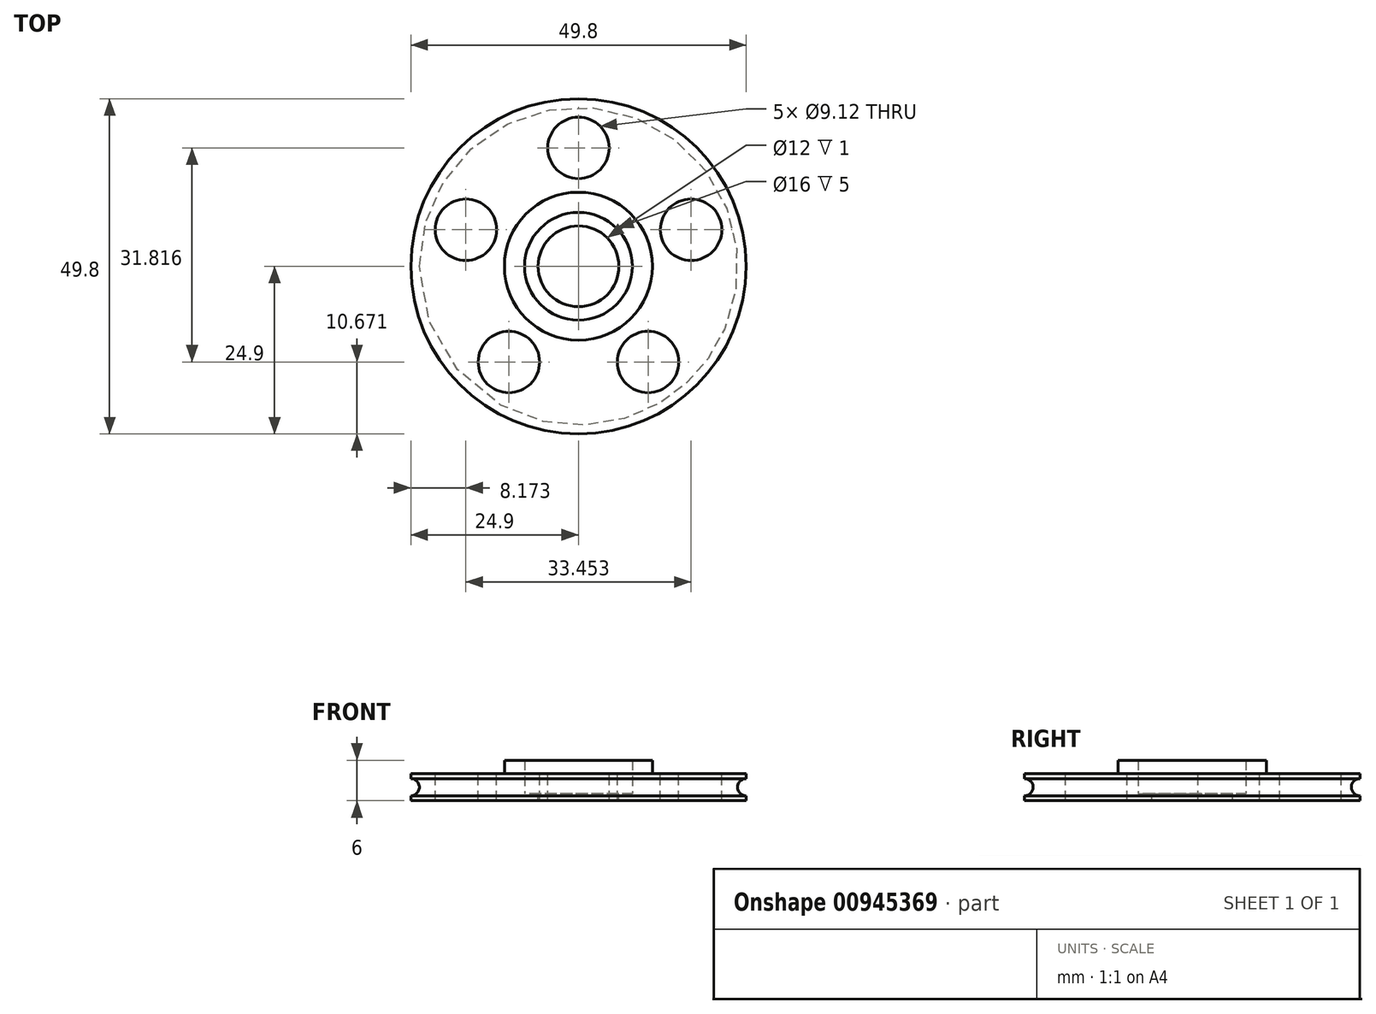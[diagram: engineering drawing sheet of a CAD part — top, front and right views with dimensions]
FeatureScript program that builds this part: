
annotation { "Feature Type Name" : "Feature", "Feature Type Description" : "" }
export const myFeature = defineFeature(function(context is Context, id is Id, definition is map)
    precondition{}
    {
        {
            var Q0;
            Q0=qCreatedBy(makeId("Top.planeOp"),FACE);
            var sketch = newSketch(context, id + "F0", { "sketchPlane" : qUnion([Q0])});
            skCircle(sketch, "E0", {"center": v(0, 0) * mm, "radius": 24.9 * mm});
            skSolve(sketch);
        }
        {
            var Q0;
            Q0=makeQuery(id+"F0.imprint","IMPRINT",FACE,{"disambiguationData":[TD([[makeQuery(id+"F0.imprint","IMPRINT",EDGE,{"derivedFrom":sQuery(id+"F0.wireOp",EDGE,"E0")}),1.0]])]});
            extrude(context, id + "F1", {"entities" : qUnion([Q0]), "depth" : 4 * mm, "offsetDistance" : 25.4 * mm});
        }
        {
            var Q0;
            Q0=makeQuery(id+"F1.opExtrude","CAP_FACE",FACE,{"disambiguationData":[OSD([sQuery(id+"F0.wireOp",EDGE,"E0"),sQuery(id+"F0.wireOp",EDGE,"n39IqKt5-bk1q-LU1x-fgod-8OyBNiFTd7FZ")])],"isStart":false});
            var sketch = newSketch(context, id + "F2", { "sketchPlane" : qUnion([Q0])});
            skCircle(sketch, "E1", {"center": v(0, 0) * mm, "radius": 8 * mm});
            skCircle(sketch, "E2.0", {"center": v(0, 0) * mm, "radius": 11 * mm});
            skSolve(sketch);
        }
        {
            var Q0;
            Q0=qSketchRegion(id+"F2",true);
            extrude(context, id + "F3", {"entities" : qUnion([Q0]), "operationType" : NewBodyOperationType.ADD, "depth" : 2 * mm, "offsetDistance" : 25.4 * mm});
        }
        {
            var Q0;
            Q0=makeQuery(id+"F3.boolean.opBoolean","SPLIT",FACE,{"disambiguationData":[TD([makeQuery(id+"F3.opExtrude","SWEPT_FACE",FACE,{"disambiguationData":[OSD([sQuery(id+"F2.wireOp",EDGE,"E1")])]})])],"derivedFrom":makeQuery(id+"F1.opExtrude","CAP_FACE",FACE,{"disambiguationData":[OSD([sQuery(id+"F0.wireOp",EDGE,"E0")])],"isStart":false})});
            var sketch = newSketch(context, id + "F4", { "sketchPlane" : qUnion([Q0])});
            skCircle(sketch, "E3", {"center": v(0, 0) * mm, "radius": 6 * mm});
            skSolve(sketch);
        }
        {
            var Q0;
            Q0=makeQuery(id+"F4.imprint","IMPRINT",FACE,{"disambiguationData":[TD([[makeQuery(id+"F4.imprint","IMPRINT",EDGE,{"derivedFrom":sQuery(id+"F4.wireOp",EDGE,"E3")}),1.0]])]});
            var Q1;
            Q1=makeQuery(id+"F4.imprint","IMPRINT",FACE,{"disambiguationData":[TD([[makeQuery(id+"F4.imprint","IMPRINT",EDGE,{"derivedFrom":makeQuery(id+"FgYK8jIepfClWtA_1.opExtrude","CAP_EDGE",EDGE,{"disambiguationData":[OSD([sQuery(id+"F8DXjnVyigKkjng_1.wireOp",EDGE,"EUjAMsCd-Zx2B-3j4q-cP5o-T3GrjTijNDqK")])],"isStart":false})}),1.0]])]});
            extrude(context, id + "F5", {"entities" : qUnion([Q0, Q1]), "operationType" : NewBodyOperationType.REMOVE, "oppositeDirection" : true, "depth" : 9 * mm, "offsetDistance" : 25.4 * mm});
        }
        {
            var Q0;
            Q0=qCreatedBy(makeId("Front.planeOp"),FACE);
            var sketch = newSketch(context, id + "F6", { "sketchPlane" : qUnion([Q0])});
            skCircle(sketch, "E4", {"center": v(-27.3, 2) * mm, "radius": 1.5 * mm});
            skLineSegment(sketch, "E5.bottom", {"start": v(-25.8, 0.65) * mm, "end": v(-27.95, 0.65) * mm});
            skLineSegment(sketch, "E5.top", {"start": v(-25.8, 3.35) * mm, "end": v(-27.95, 3.35) * mm});
            skLineSegment(sketch, "E5.left", {"start": v(-25.8, 0.65) * mm, "end": v(-25.8, 3.35) * mm});
            skLineSegment(sketch, "E5.right", {"start": v(-28.8, 1.91) * mm, "end": v(-28.8, 2.09) * mm});
            skLineSegment(sketch, "E6", {"start": v(0, 19.1) * mm, "end": v(0, -12.61) * mm, "construction": true});
            skLineSegment(sketch, "E7", {"start": v(-25.8, 1.83) * mm, "end": v(-25.81, 1.83) * mm});
            skPoint(sketch, "E8.orphan", {"position": v(-38.97, 3.35) * mm});
            skPoint(sketch, "E9.end.orphan", {"position": v(-15.64, 0.65) * mm});
            skPoint(sketch, "E9.start.orphan", {"position": v(-25.8, 2) * mm});
            skSolve(sketch);
        }
        {
            var Q0;
            {var subQ0=sQuery(id+"F6.wireOp",EDGE,"E5.top");var subQ1=sQuery(id+"F6.wireOp",EDGE,"E4");var subQ2=makeQuery(id+"F6.imprint","INTERSECT",VERTEX,{"disambiguationData":[OD(0.0)],"derivedFrom":[subQ1,subQ0]});Q0=makeQuery(id+"F6.imprint","IMPRINT",FACE,{"disambiguationData":[TD([[makeQuery(id+"F6.imprint","IMPRINT",EDGE,{"disambiguationData":[TD([[subQ2,1.0]])],"derivedFrom":subQ1}),1.0]])]});}
            var Q1;
            {var subQ0=sQuery(id+"F6.wireOp",EDGE,"E5.bottom");var subQ1=sQuery(id+"F6.wireOp",EDGE,"E4");var subQ2=makeQuery(id+"F6.imprint","INTERSECT",VERTEX,{"disambiguationData":[OD(0.0)],"derivedFrom":[subQ1,subQ0]});Q1=makeQuery(id+"F6.imprint","IMPRINT",FACE,{"disambiguationData":[TD([[makeQuery(id+"F6.imprint","IMPRINT",EDGE,{"disambiguationData":[TD([[subQ2,-1.0]])],"derivedFrom":subQ1}),1.0]])]});}
            var Q2;
            {var subQ4=sQuery(id+"F6.wireOp",EDGE,"E5.right");Q2=makeQuery(id+"F6.imprint","IMPRINT",FACE,{"disambiguationData":[TD([[makeQuery(id+"F6.imprint","IMPRINT",EDGE,{"derivedFrom":subQ4}),-1.0]])]});}
            var Q3;
            {var subQ0=sQuery(id+"F6.wireOp",EDGE,"p3G3spWP-JurA-dj01-Cwvm-HHlCDoPDIoxd");Q3=makeQuery(id+"F6.imprint","IMPRINT",FACE,{"disambiguationData":[TD([[makeQuery(id+"F6.imprint","IMPRINT",EDGE,{"derivedFrom":subQ0}),1.0]])]});}
            var Q4;
            Q4=makeQuery(id+"F6.imprint","IMPRINT",FACE,{"disambiguationData":[TD([[makeQuery(id+"F6.imprint","IMPRINT",EDGE,{"derivedFrom":sQuery(id+"F6.wireOp",EDGE,"p3G3spWP-JurA-dj01-Cwvm-HHlCDoPDIoxd")}),-1.0]])]});
            var Q5;
            {var subQ0=sQuery(id+"F6.wireOp",EDGE,"E9");Q5=makeQuery(id+"F6.imprint","IMPRINT",FACE,{"disambiguationData":[TD([[makeQuery(id+"F6.imprint","IMPRINT",EDGE,{"derivedFrom":subQ0}),1.0]])]});}
            var Q6;
            Q6=sQuery(id+"F6.wireOp",EDGE,"E6");
            revolve(context, id + "F7", {"operationType" : NewBodyOperationType.REMOVE, "surfaceOperationType" : NewSurfaceOperationType.NEW, "entities" : qUnion([Q0, Q1, Q2, Q3, Q4, Q5]), "axis" : qUnion([Q6]), "revolveType" : RevolveType.FULL, "oppositeDirection" : true});
        }
        {
            var Q0;
            Q0=makeQuery(id+"F3.boolean.opBoolean","SPLIT",FACE,{"disambiguationData":[TD([makeQuery(id+"F3.opExtrude","SWEPT_FACE",FACE,{"disambiguationData":[OSD([sQuery(id+"F2.wireOp",EDGE,"E1")])]})])],"derivedFrom":makeQuery(id+"F1.opExtrude","CAP_FACE",FACE,{"disambiguationData":[OSD([sQuery(id+"F0.wireOp",EDGE,"E0")])],"isStart":false})});
            extrude(context, id + "F8", {"entities" : qUnion([Q0]), "operationType" : NewBodyOperationType.REMOVE, "oppositeDirection" : true, "depth" : 3 * mm, "offsetDistance" : 25 * mm});
        }
        {
            var Q0;
            Q0=qCreatedBy(makeId("Front.planeOp"),FACE);
            var sketch = newSketch(context, id + "F9", { "sketchPlane" : qUnion([Q0])});
            skLineSegment(sketch, "E10", {"start": v(-24.92, 4) * mm, "end": v(-24.92, 0) * mm});
            skCircle(sketch, "E11", {"center": v(-24.92, 2) * mm, "radius": 1.28 * mm});
            skLineSegment(sketch, "E12", {"start": v(0, 9.34) * mm, "end": v(0, -3.6) * mm, "construction": true});
            skSolve(sketch);
        }
        {
            var Q0;
            {var subQ0=sQuery(id+"F9.wireOp",EDGE,"E11");var subQ1=sQuery(id+"F9.wireOp",EDGE,"E10");var subQ2=makeQuery(id+"F9.imprint","INTERSECT",VERTEX,{"disambiguationData":[OD(0.0)],"derivedFrom":[subQ1,subQ0]});Q0=makeQuery(id+"F9.imprint","IMPRINT",FACE,{"disambiguationData":[TD([[makeQuery(id+"F9.imprint","IMPRINT",EDGE,{"disambiguationData":[TD([[subQ2,1.0]])],"derivedFrom":subQ1}),1.0]])]});}
            var Q1;
            {var subQ0=sQuery(id+"F9.wireOp",EDGE,"E11");var subQ1=sQuery(id+"F9.wireOp",EDGE,"E10");var subQ2=makeQuery(id+"F9.imprint","INTERSECT",VERTEX,{"disambiguationData":[OD(0.0)],"derivedFrom":[subQ1,subQ0]});Q1=makeQuery(id+"F9.imprint","IMPRINT",FACE,{"disambiguationData":[TD([[makeQuery(id+"F9.imprint","IMPRINT",EDGE,{"disambiguationData":[TD([[subQ2,1.0]])],"derivedFrom":subQ1}),-1.0]])]});}
            var Q2;
            Q2=sQuery(id+"F9.wireOp",EDGE,"E12");
            revolve(context, id + "F10", {"operationType" : NewBodyOperationType.REMOVE, "surfaceOperationType" : NewSurfaceOperationType.NEW, "entities" : qUnion([Q0, Q1]), "axis" : qUnion([Q2]), "revolveType" : RevolveType.FULL, "oppositeDirection" : true});
        }
        {
            var Q0;
            {var subQ1=sQuery(id+"F0.wireOp",EDGE,"E0");var subQ2=makeQuery(id+"F1.opExtrude","SWEPT_FACE",FACE,{"disambiguationData":[OSD([subQ1])]});Q0=makeQuery(id+"FvaswZWDLJZ7FP9_1.boolean.opBoolean","SPLIT",FACE,{"disambiguationData":[TD([subQ2])],"derivedFrom":makeQuery(id+"F3.boolean.opBoolean","SPLIT",FACE,{"disambiguationData":[TD([subQ2])],"derivedFrom":makeQuery(id+"F1.opExtrude","CAP_FACE",FACE,{"disambiguationData":[OSD([subQ1])],"isStart":false})})});}
            var sketch = newSketch(context, id + "F11", { "sketchPlane" : qUnion([Q0])});
            skCircle(sketch, "E13", {"center": v(0, 17.59) * mm, "radius": 4.56 * mm});
            skCircle(sketch, "E14.1.0", {"center": v(-16.73, 5.43) * mm, "radius": 4.56 * mm});
            skCircle(sketch, "E14.2.0", {"center": v(-10.34, -14.23) * mm, "radius": 4.56 * mm});
            skCircle(sketch, "E14.3.0", {"center": v(10.34, -14.23) * mm, "radius": 4.56 * mm});
            skCircle(sketch, "E14.4.0", {"center": v(16.73, 5.43) * mm, "radius": 4.56 * mm});
            skPoint(sketch, "E14.center", {"position": v(0, 0) * mm});
            skSolve(sketch);
        }
        {
            var Q0;
            Q0=makeQuery(id+"F11.imprint","IMPRINT",FACE,{"disambiguationData":[TD([[makeQuery(id+"F11.imprint","IMPRINT",EDGE,{"derivedFrom":sQuery(id+"F11.wireOp",EDGE,"E13")}),1.0]])]});
            var Q1;
            Q1=makeQuery(id+"F11.imprint","IMPRINT",FACE,{"disambiguationData":[TD([[makeQuery(id+"F11.imprint","IMPRINT",EDGE,{"derivedFrom":sQuery(id+"F11.wireOp",EDGE,"E14.1.0")}),1.0]])]});
            var Q2;
            Q2=makeQuery(id+"F11.imprint","IMPRINT",FACE,{"disambiguationData":[TD([[makeQuery(id+"F11.imprint","IMPRINT",EDGE,{"derivedFrom":sQuery(id+"F11.wireOp",EDGE,"E14.2.0")}),1.0]])]});
            var Q3;
            Q3=makeQuery(id+"F11.imprint","IMPRINT",FACE,{"disambiguationData":[TD([[makeQuery(id+"F11.imprint","IMPRINT",EDGE,{"derivedFrom":sQuery(id+"F11.wireOp",EDGE,"E14.3.0")}),1.0]])]});
            var Q4;
            Q4=makeQuery(id+"F11.imprint","IMPRINT",FACE,{"disambiguationData":[TD([[makeQuery(id+"F11.imprint","IMPRINT",EDGE,{"derivedFrom":sQuery(id+"F11.wireOp",EDGE,"E14.4.0")}),1.0]])]});
            var Q5;
            Q5=makeQuery(id+"F11.imprint","IMPRINT",FACE,{"disambiguationData":[TD([[makeQuery(id+"F11.imprint","IMPRINT",EDGE,{"derivedFrom":sQuery(id+"F11.wireOp",EDGE,"8a64cefe-6ebd-494f-8c58-59fa29c1fc96.1.6.0")}),1.0]])]});
            var Q6;
            Q6=makeQuery(id+"F11.imprint","IMPRINT",FACE,{"disambiguationData":[TD([[makeQuery(id+"F11.imprint","IMPRINT",EDGE,{"derivedFrom":sQuery(id+"F11.wireOp",EDGE,"8a64cefe-6ebd-494f-8c58-59fa29c1fc96.1.5.0")}),1.0]])]});
            extrude(context, id + "F12", {"entities" : qUnion([Q0, Q1, Q2, Q3, Q4, Q5, Q6]), "operationType" : NewBodyOperationType.REMOVE, "oppositeDirection" : true, "depth" : 25 * mm, "offsetDistance" : 25 * mm});
        }
    });
